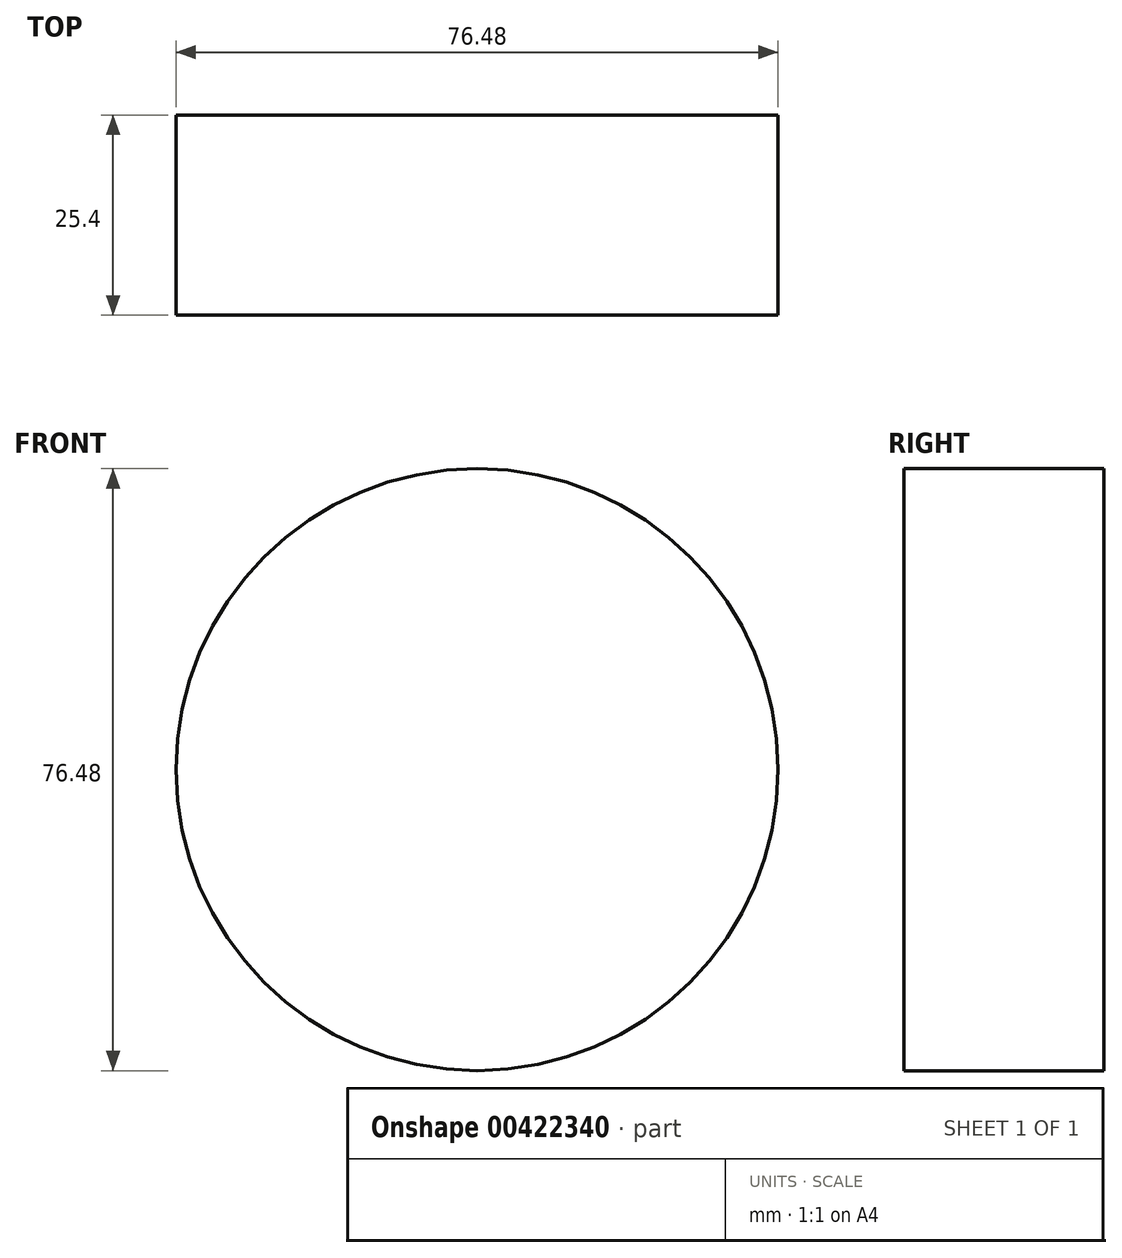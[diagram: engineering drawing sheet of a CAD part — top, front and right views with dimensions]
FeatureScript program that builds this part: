
annotation { "Feature Type Name" : "Feature", "Feature Type Description" : "" }
export const myFeature = defineFeature(function(context is Context, id is Id, definition is map)
    precondition{}
    {
        {
            var Q0;
            Q0=qCreatedBy(makeId("Front.planeOp"),FACE);
            var sketch = newSketch(context, id + "F0", { "sketchPlane" : qUnion([Q0])});
            skCircle(sketch, "E0", {"center": v(0, 0) * mm, "radius": 38.24 * mm});
            skSolve(sketch);
        }
        {
            var Q0;
            Q0 = qSketchRegion(id + "F0", true);
            extrude(context, id + "F1", {"entities" : qUnion([Q0]), "depth" : 25.4 * mm});
        }
    });
